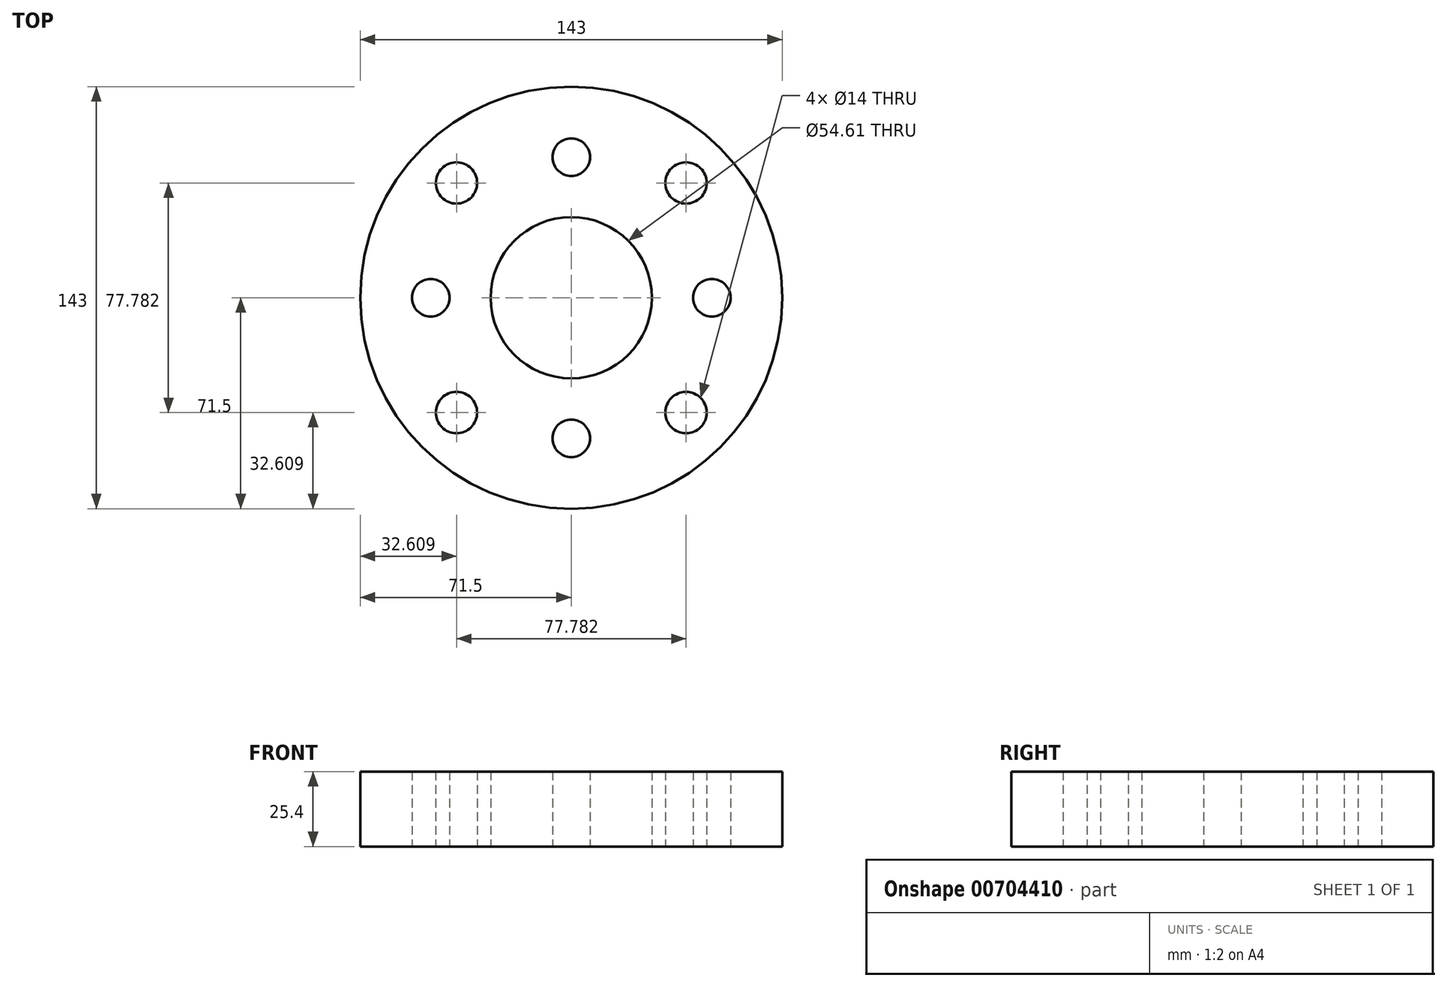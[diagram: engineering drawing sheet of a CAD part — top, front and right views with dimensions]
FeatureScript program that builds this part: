
annotation { "Feature Type Name" : "Feature", "Feature Type Description" : "" }
export const myFeature = defineFeature(function(context is Context, id is Id, definition is map)
    precondition{}
    {
        {
            var Q0;
            Q0=qCreatedBy(makeId("Top.planeOp"),FACE);
            var sketch = newSketch(context, id + "F0", { "sketchPlane" : qUnion([Q0])});
            skCircle(sketch, "E0", {"center": v(0, 0) * mm, "radius": 27.3 * mm});
            skCircle(sketch, "E1", {"center": v(0, 0) * mm, "radius": 71.5 * mm});
            skCircle(sketch, "E2", {"center": v(0, 47.63) * mm, "radius": 6.35 * mm});
            skCircle(sketch, "E3", {"center": v(47.63, 0) * mm, "radius": 6.35 * mm});
            skCircle(sketch, "E4", {"center": v(0, -47.63) * mm, "radius": 6.35 * mm});
            skCircle(sketch, "E5", {"center": v(-47.63, 0) * mm, "radius": 6.35 * mm});
            skLineSegment(sketch, "E6", {"start": v(0, 0) * mm, "end": v(-47.63, 0) * mm, "construction": true});
            skLineSegment(sketch, "E7", {"start": v(0, 0) * mm, "end": v(0, 47.63) * mm, "construction": true});
            skLineSegment(sketch, "E8", {"start": v(0, 0) * mm, "end": v(47.63, 0) * mm, "construction": true});
            skLineSegment(sketch, "E9", {"start": v(0, 0) * mm, "end": v(0, -47.63) * mm, "construction": true});
            skLineSegment(sketch, "E10", {"start": v(0, 0) * mm, "end": v(38.9, 38.9) * mm, "construction": true});
            skLineSegment(sketch, "E11", {"start": v(0, 0) * mm, "end": v(-38.9, -38.9) * mm, "construction": true});
            skLineSegment(sketch, "E12", {"start": v(0, 0) * mm, "end": v(-38.9, 38.9) * mm, "construction": true});
            skLineSegment(sketch, "E13", {"start": v(0, 0) * mm, "end": v(38.9, -38.9) * mm, "construction": true});
            skCircle(sketch, "E14", {"center": v(-38.9, 38.9) * mm, "radius": 7 * mm});
            skCircle(sketch, "E15", {"center": v(38.9, 38.9) * mm, "radius": 7 * mm});
            skCircle(sketch, "E16", {"center": v(38.9, -38.9) * mm, "radius": 7 * mm});
            skCircle(sketch, "E17", {"center": v(-38.9, -38.9) * mm, "radius": 7 * mm});
            skSolve(sketch);
        }
        {
            var Q0;
            Q0 = qSketchRegion(id + "F0", true);
            extrude(context, id + "F1", {"entities" : qUnion([Q0]), "depth" : 25.4 * mm, "offsetDistance" : 25.4 * mm});
        }
    });
